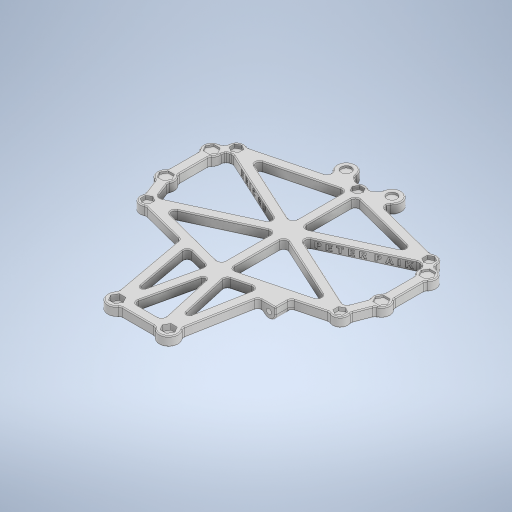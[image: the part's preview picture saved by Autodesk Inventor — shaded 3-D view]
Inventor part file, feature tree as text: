
AUTODESK INVENTOR PART (.ipt)
format: ipt  version: 2024.2 (Build 282272000, 272)  size: 1,595,392 bytes
history: native  units: in
note: dims shown in document units (in); Inventor stores cm internally (conversion verified against a paired STEP export)
features: extrude x11, sketch x10, fillet x3, hole x2, emboss x2, projected_geometry x1
ambient origin geometry x8: Origin, YZ Plane, XZ Plane, XY Plane, X Axis, Y Axis, Z Axis, Center Point
bodies: Solid1 (feature_tree)
feature tree (29):
  sketch  "Sketch1"  dims[d1=0.122in d2=1.9291in]
  extrude  "Extrusion1"  Depth=1.9291in
  sketch  "Sketch2"  dims[d3=2.4409in d5=0.2067in]
  extrude  "Extrusion2"  Depth=0.2067in
  extrude  "Extrusion3"  Depth=0.3937in
  sketch  "Sketch4"  dims[d6=0.2067in d7=0.3937in]
  extrude  "Extrusion4"  Depth=3.9764in
  extrude  "Extrusion10"  Depth=0.1969in
  hole  "Hole2"  [1 undecoded]
  extrude  "Extrusion6"  Depth=0.0984in
  sketch  "Sketch5"  dims[d13=0.5118in d14=3.9764in]
  hole  "Hole1"  [1 undecoded]
  extrude  "Extrusion12"  Depth=0.1969in
  extrude  "Extrusion5"  Depth=0.0098in
  fillet  "Fillet1"  Radius=0.1969in
  fillet  "Fillet2"  Radius=0.0984in
  fillet  "Fillet3"  Radius=0.0984in
  extrude  "Extrusion7"  Depth=0.0098in
  extrude  "Extrusion8"  Depth=0.0098in
  extrude  "Extrusion9"  Depth=0.0098in
  sketch  "Sketch10"  dims[d22=0.0984in d23=0.0984in]
  sketch  "Sketch11"  dims[d24=0.0984in d25=0.1969in]
  emboss  "Emboss1"
  emboss  "Emboss2"
  projected_geometry  "Projected Loop1"
  sketch  "Sketch6"  dims[d15=1.9882in d17=0.1969in]
  sketch  "Sketch7"  dims[d18=0.1969in d19=0.1969in]
  sketch  "Sketch8"  dims[d20=0.0984in d21=0.0984in]
  sketch  "Sketch14"  dims[d26=0.0984in d27=0.0984in d30=0.1969in d31=0.0984in d32=0.0984in d35=0.2244in d36=0.9449in d37=0.315in d38=0.1929in d39=2.9528in d40=0.6063in d41=0.1969in d42=0.1969in d43=0.0984in d44=0.0984in d48=1.2598in d49=1.063in d51=0.2362in d52=0.2362in d53=0.1969in d55=0.1969in d56=0.1969in d57=0.1969in d66=0.3543in d67=0.1969in d68=0.0984in d69=0.1969in d70=0.0984in d71=0.0984in d72=0.1969in d73=0.0984in d74=0.0984in d75=0.1969in d76=0.0984in d77=0.0984in d78=0.1969in d79=0.0984in d80=0.1969in d81=0.0984in d82=0.3937in d83=0.1969in d84=0.0984in d85=1.5748in d86=0.0984in d87=0.0984in d88=0.1969in d89=0.0in d90=0.4466in d91=0.4466in d92=0.9449in d93=0.3937in d94=0.0984in d95=0.4724in d96=0.2362in d97=0.0984in d100=0.0984in d101=0.0984in d102=0.1969in d103=0.0in d104=0.0748in d105=0.0in d106=0.0394in d107=0.0in d108=0.1083in d110=0.315in d111=0.0in d112=0.2067in d113=0.1339in d114=0.2362in d115=0.1575in d116=0.0787in d117=90.0deg d118=0.0787in d119=0.8108in d120=0.0394in d121=0.0in d122=0.1181in d123=0.0in d124=0.0787in d125=0.0787in d127=0.0197in d128=0.0984in d129=0.7874in d130=0.1378in d131=0.1083in d132=0.2362in d133=0.1575in d134=0.0787in d135=90.0deg d136=0.2362in d137=0.0in d138=0.0079in d139=0.0in d140=0.0079in d141=0.0in d142=0.0079in d143=0.0in d144=0.1378in d145=0.1378in d146=0.0079in d147=0.0in d148=0.0098in d149=0.0in d150=0.0098in d151=0.0in d154=0.0492in d155=0.2067in d156=0.0394in d157=0.0in]
note: 2 required parameter values undecoded (feature->parameter linkage not recoverable at this tier; creation-order binding heuristic only, values carry confidence <= 0.55)
